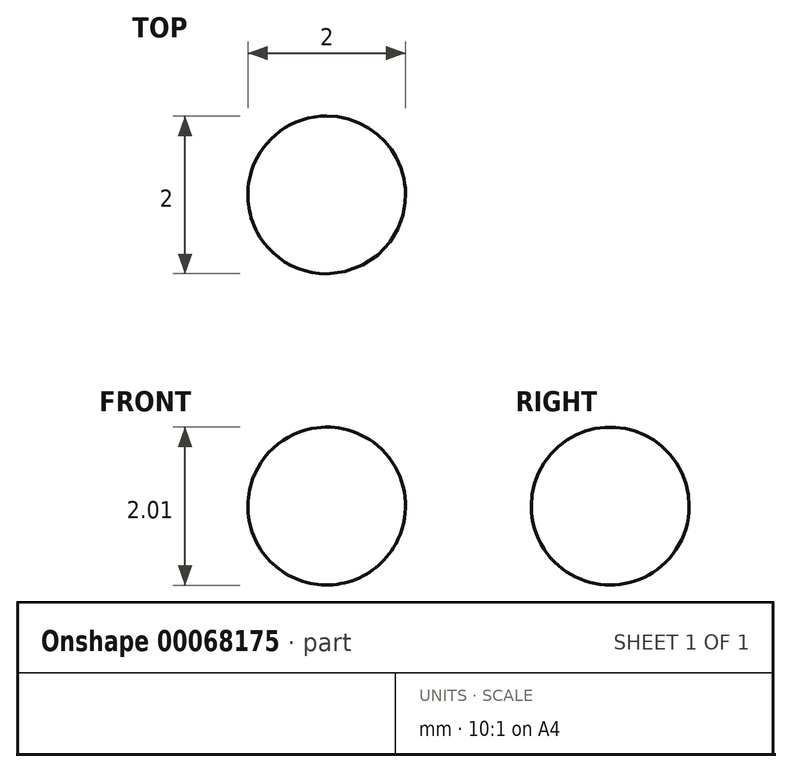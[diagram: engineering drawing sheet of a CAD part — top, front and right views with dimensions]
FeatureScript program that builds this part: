
annotation { "Feature Type Name" : "Feature", "Feature Type Description" : "" }
export const myFeature = defineFeature(function(context is Context, id is Id, definition is map)
    precondition{}
    {
        {
            var Q0;
            Q0=qCreatedBy(makeId("Front.planeOp"),FACE);
            var sketch = newSketch(context, id + "F0", { "sketchPlane" : qUnion([Q0])});
            skCircle(sketch, "E0", {"center": v(0, 0) * mm, "radius": 1 * mm});
            skLineSegment(sketch, "E1", {"start": v(0.87, -0.48) * mm, "end": v(-0.88, 0.48) * mm});
            skSolve(sketch);
        }
        {
            var Q0;
            {var subQ0=sQuery(id+"F0.wireOp",EDGE,"E1");Q0=makeQuery(id+"F0.imprint","IMPRINT",FACE,{"disambiguationData":[TD([[makeQuery(id+"F0.imprint","IMPRINT",EDGE,{"derivedFrom":subQ0}),-1.0]])]});}
            var Q1;
            Q1=sQuery(id+"F0.wireOp",EDGE,"E1");
            revolve(context, id + "F1", {"entities" : qUnion([Q0]), "axis" : qUnion([Q1]), "revolveType" : RevolveType.FULL});
        }
    });
